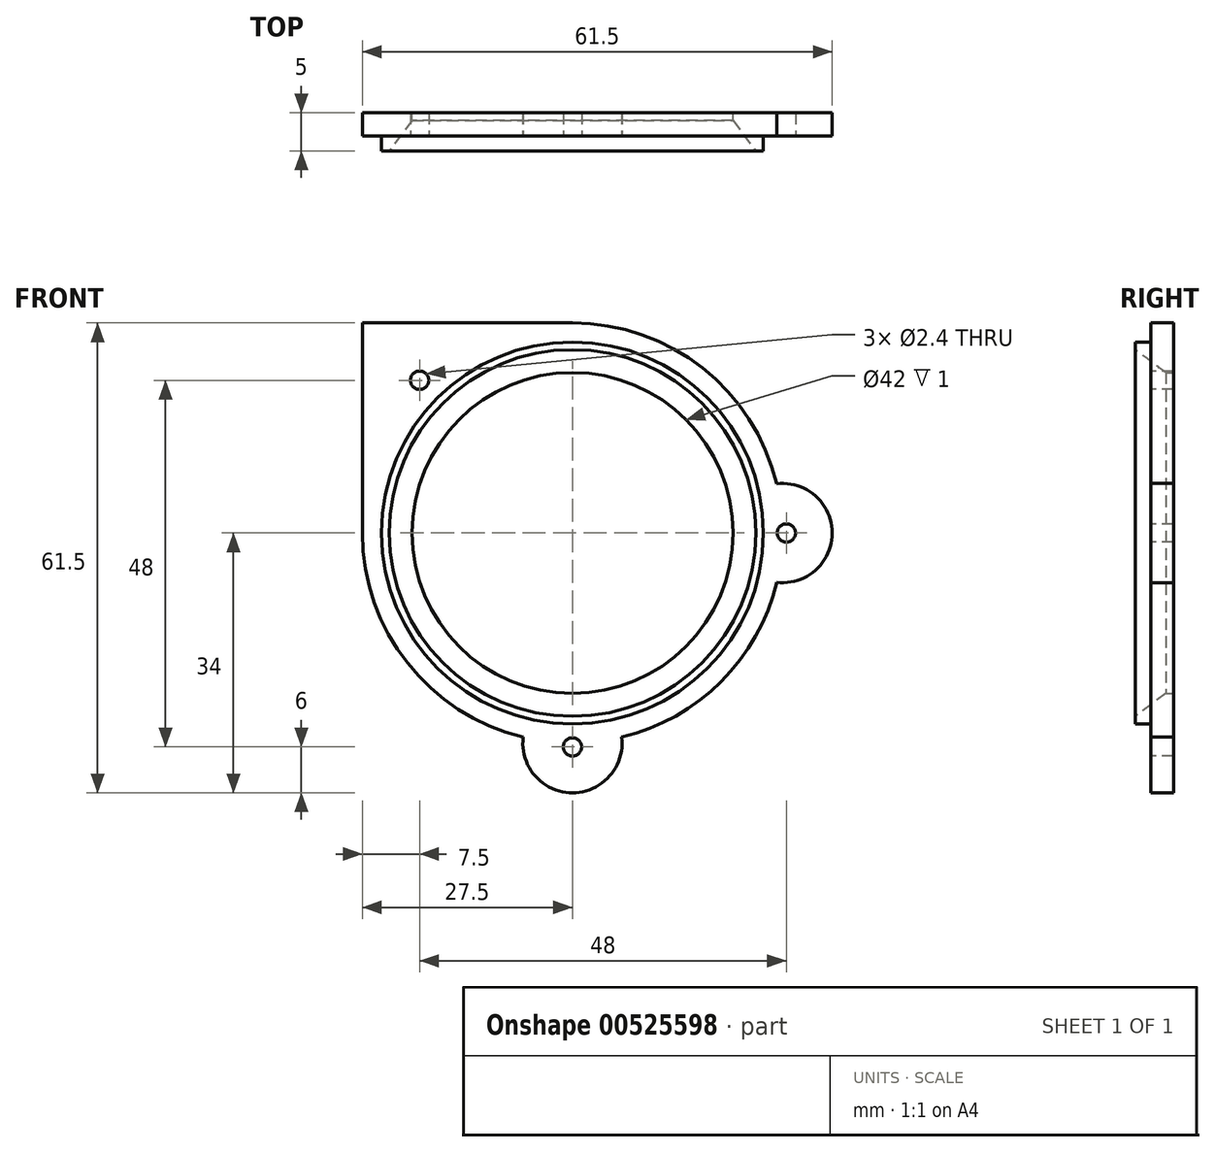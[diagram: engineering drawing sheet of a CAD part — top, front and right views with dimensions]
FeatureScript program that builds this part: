
annotation { "Feature Type Name" : "Feature", "Feature Type Description" : "" }
export const myFeature = defineFeature(function(context is Context, id is Id, definition is map)
    precondition{}
    {
        {
            var Q0;
            Q0=qCreatedBy(makeId("Right.planeOp"),FACE);
            var sketch = newSketch(context, id + "F0", { "sketchPlane" : qUnion([Q0])});
            skLineSegment(sketch, "E0", {"start": v(19.32, 0) * mm, "end": v(-16.11, 0) * mm, "construction": true});
            skLineSegment(sketch, "E1", {"start": v(-3, 25) * mm, "end": v(-3, 24) * mm});
            skLineSegment(sketch, "E2", {"start": v(2, 21) * mm, "end": v(2, 25) * mm});
            skLineSegment(sketch, "E3", {"start": v(2, 25) * mm, "end": v(-3, 25) * mm});
            skLineSegment(sketch, "E4", {"start": v(2, 21) * mm, "end": v(1, 21) * mm});
            skLineSegment(sketch, "E5", {"start": v(1, 21) * mm, "end": v(-3, 24) * mm});
            skSolve(sketch);
        }
        {
            var Q0;
            Q0=qSketchRegion(id+"F0",true);
            var Q1;
            Q1=sQuery(id+"F0.wireOp",EDGE,"E0");
            revolve(context, id + "F1", {"entities" : qUnion([Q0]), "axis" : qUnion([Q1]), "revolveType" : RevolveType.FULL});
        }
        {
            var Q0;
            Q0=makeQuery(id+"F1.opRevolve","SWEPT_FACE",FACE,{"disambiguationData":[OSD([sQuery(id+"F0.wireOp",EDGE,"E1")])]});
            cPlane(context, id + "F2", {"entities" : qUnion([Q0]), "cplaneType" : CPlaneType.OFFSET, "offset" : 2 * mm, "oppositeDirection" : true, "width" : 150 * mm, "height" : 150 * mm});
        }
        {
            var Q0;
            Q0=qCreatedBy(id+"F2.planeOp",FACE);
            var sketch = newSketch(context, id + "F3", { "sketchPlane" : qUnion([Q0])});
            skPoint(sketch, "E6.middle", {"position": v(0, 0) * mm});
            skCircle(sketch, "E7", {"center": v(-20, 20) * mm, "radius": 1.2 * mm});
            skCircle(sketch, "E8", {"center": v(-20, -20) * mm, "radius": 1.2 * mm, "construction": true});
            skCircle(sketch, "E9", {"center": v(20, -20) * mm, "radius": 1.2 * mm, "construction": true});
            skCircle(sketch, "E10", {"center": v(20, 20) * mm, "radius": 1.2 * mm, "construction": true});
            skLineSegment(sketch, "E11.top", {"start": v(0, 27.5) * mm, "end": v(-27.5, 27.5) * mm});
            skLineSegment(sketch, "E11.right", {"start": v(-27.5, 0) * mm, "end": v(-27.5, 27.5) * mm});
            skCircle(sketch, "E12", {"center": v(0, 0) * mm, "radius": 25 * mm});
            skArc(sketch, "E13", {"start": v(-27.5, 0) * mm, "mid": v(19.45, -19.45) * mm, "end": v(0, 27.5) * mm});
            skArc(sketch, "E14", {"start": v(26.73, 6.45) * mm, "mid": v(34, 0) * mm, "end": v(26.73, -6.45) * mm});
            skCircle(sketch, "E15", {"center": v(28, 0) * mm, "radius": 1.2 * mm});
            skArc(sketch, "E16", {"start": v(6.45, -26.73) * mm, "mid": v(0, -34) * mm, "end": v(-6.45, -26.73) * mm});
            skCircle(sketch, "E17", {"center": v(0, -28) * mm, "radius": 1.2 * mm});
            skSolve(sketch);
        }
        {
            var Q0;
            Q0=qSketchRegion(id+"F3",true);
            extrude(context, id + "F4", {"entities" : qUnion([Q0]), "operationType" : NewBodyOperationType.ADD, "oppositeDirection" : true, "depth" : 3 * mm, "offsetDistance" : 25 * mm});
        }
    });
